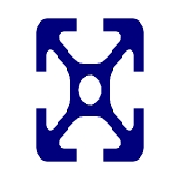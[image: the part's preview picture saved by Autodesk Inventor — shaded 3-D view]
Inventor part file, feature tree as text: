
AUTODESK INVENTOR PART (.ipt)
format: ipt  version: 2020 (Build 240168000, 168)  size: 272,896 bytes
history: native  units: mm
features: other x16, sketch x8, plane x2, split x2
ambient origin geometry x8: Origin, YZ Plane, XZ Plane, XY Plane, X Axis, Y Axis, Z Axis, Center Point
bodies: Body (feature_tree)
feature tree (28):
  other  "Řízená délka"
  other  "Těleso1"
  other  "Start Plane"
  other  "End Plane"
  other  "iFeatureSketch"
  other  "DRAZKA_20:1"
  other  "DRAZKA_20:2"
  other  "DRAZKA_20:3"
  other  "DRAZKA_20:4"
  other  "DIRA_20:1"
  other  "DRAZKA_20:1Axis"
  other  "DRAZKA_20:2Axis"
  other  "DRAZKA_20:3Axis"
  other  "DRAZKA_20:4Axis"
  other  "DIRA_20:1Axis"
  plane  "Work Plane5"
  split  "Split1"
  plane  "Work Plane6"
  split  "Split2"
  sketch  "Sketch"  dims[d2=20.0mm d3=20.0mm d4=2.0mm d9=-0.0mm d10=360.0mm d11=0.13mm d12=0.0mm d15=0.83mm d16=0.83mm d17=9.8mm d18=3.0mm d19=4.55mm d20=45.0deg d21=5.2mm d22=1.8mm d24=1.0mm d26=0.83mm d27=0.83mm d28=9.8mm d29=3.0mm d30=4.55mm d31=45.0deg d32=5.2mm d33=1.8mm d35=1.0mm d37=0.83mm d38=0.83mm d39=9.8mm d40=3.0mm d41=4.55mm d42=45.0deg d43=5.2mm d44=1.8mm d46=1.0mm d48=0.83mm d49=0.83mm d50=9.8mm d51=3.0mm d52=4.55mm d53=45.0deg d54=5.2mm d55=1.8mm d57=1.0mm d59=4.3mm d60=0.0mm d61=0.0mm d62=0.0mm d63=0.0mm d64=0.0mm d65=0.0mm d66=0.0mm d67=0.0mm d76=90.0deg d14=360.0mm]
  sketch  "Náčrt11"
  other  "Pracovní rovina4"
  sketch  "Náčrt12"
  sketch  "Náčrt6"
  sketch  "Náčrt7"
  sketch  "Náčrt8"
  sketch  "Náčrt9"
  sketch  "Náčrt10"
